# Revit family: Midea_VRF_Outdoor_VR_MPanel_V6-R400(450,500)WV2RN1(50Hz) -去LOGO
name_source: partatom
category: Mechanical Equipment
revit_build: Autodesk Revit 2013 (Build: 20120221_2030(x64)
units: mm (PartAtom-declared; Revit-internal decimal feet)

## types (3) — shared parameters
Air Flow = 15800.000 m³/h
Casing color = White
Compressor = 1
Condensation = Air
Depth = 825 mm  [stored 2.70669 ft]
Description = High efficiency air cooled
Gas = R410A
Height = 1635 mm  [stored 5.36417 ft]
High Pressure Gas Pipe = 25.4 mm  [stored 0.0833333 ft]
Installation = Outdoor installation
Liquid pipe = 15.9 mm
Low Pressure Gas Pipe = 28.2 mm
Machine material = Galvanized Steel
Manufacturer = Midea
Net Weight = 291.00 kg
Series = VRF
Width = 1340 mm
clearance access behind = 1000 mm  [stored 3.28084 ft]
clearance access front = 1000 mm  [stored 3.28084 ft]
clearance access left = 1000 mm  [stored 3.28084 ft]
clearance access right = 1000 mm  [stored 3.28084 ft]

## per-type parameters (varying)
| type | Cooling Capacity | Cooling Power Input | Heating Capacity | Heating Power Input | Maximum Fuse Amps | Minimum Circuit Amps | Power supply |
| MV6-R400WV2RN1 | 40.000 kW | 9.830 kW | 40.000 kW | 8.260 kW | 30 A | 28 A | 220V 3Ph~60Hz |
| MV6-R450WV2RN1 | 45.000 kW | 12.000 kW | 45.000 kW | 9.780 kW | 35 A | 34 A | 380-415V 3N~50Hz/60Hz |
| MV6-R500WV2RN1 | 50.000 kW | 13.810 kW | 50.000 kW | 11.900 kW | 40 A | 36 A | 380-415V 3N~50Hz/60Hz |

note: column(s) folded — value = type name in every type: Model

note: [stored X ft] marks values corroborated as IEEE doubles in the binary element streams (Revit-internal decimal feet)

## geometry (parser evidence)
native form markers: Sweep x16
no freeform markers — native parametric forms only
